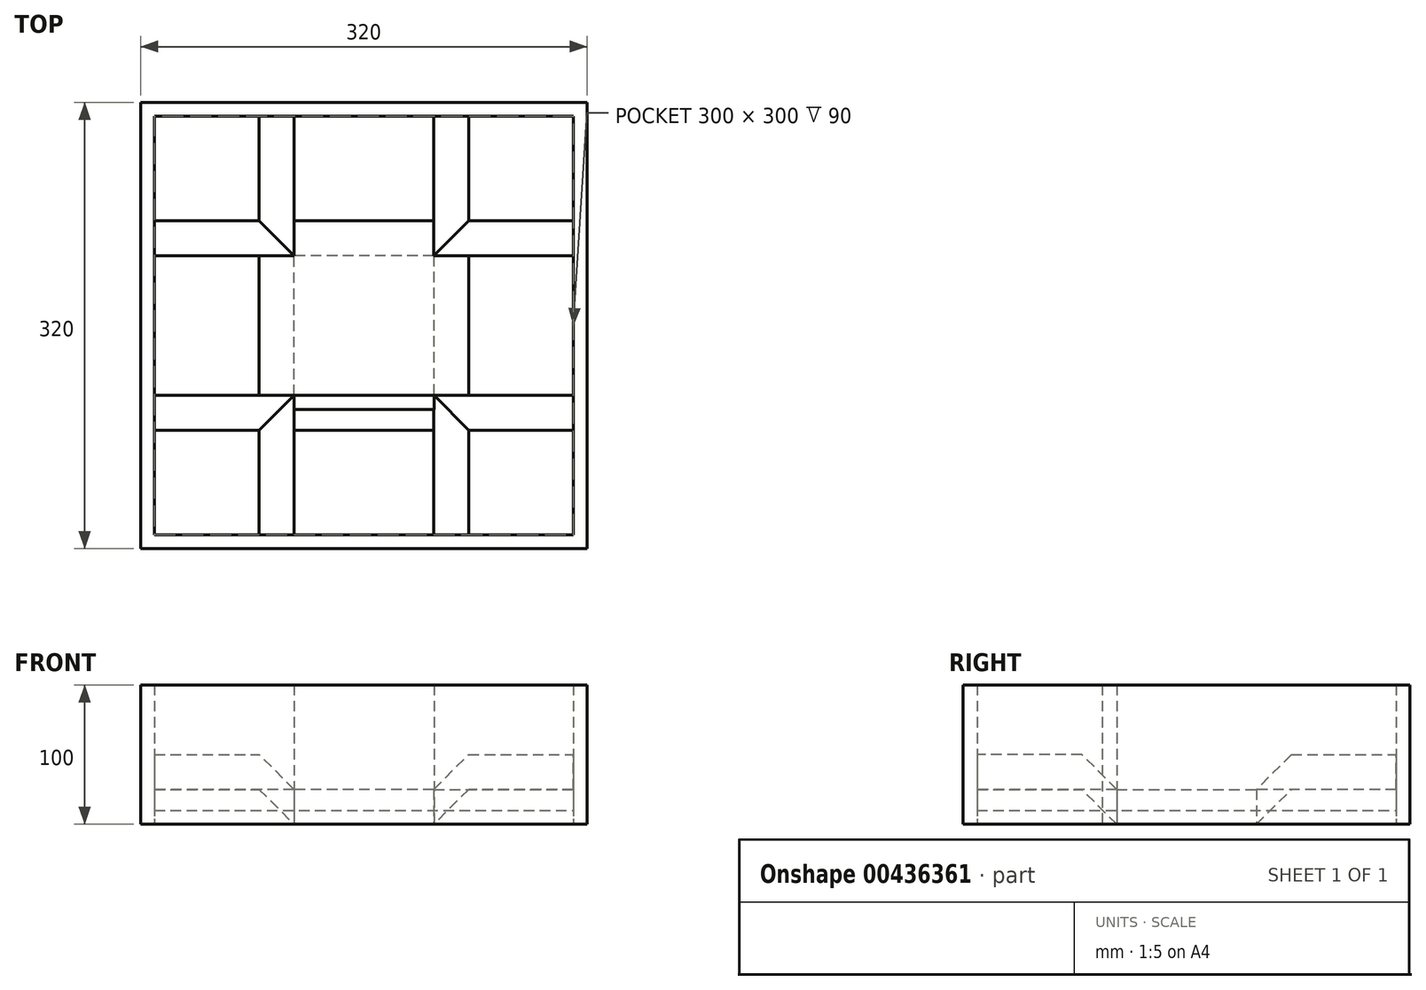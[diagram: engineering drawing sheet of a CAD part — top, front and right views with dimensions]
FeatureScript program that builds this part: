
annotation { "Feature Type Name" : "Feature", "Feature Type Description" : "" }
export const myFeature = defineFeature(function(context is Context, id is Id, definition is map)
    precondition{}
    {
        {
            var Q0;
            Q0=qCreatedBy(makeId("Top.planeOp"),FACE);
            var sketch = newSketch(context, id + "F0", { "sketchPlane" : qUnion([Q0])});
            skLineSegment(sketch, "E0", {"start": v(0, 0) * mm, "end": v(100, 0) * mm});
            skLineSegment(sketch, "E1", {"start": v(100, 0) * mm, "end": v(100, 100) * mm});
            skLineSegment(sketch, "E2", {"start": v(100, 100) * mm, "end": v(200, 100) * mm});
            skLineSegment(sketch, "E3", {"start": v(200, 100) * mm, "end": v(200, 0) * mm});
            skLineSegment(sketch, "E4", {"start": v(200, 0) * mm, "end": v(300, 0) * mm});
            skLineSegment(sketch, "E5", {"start": v(300, 0) * mm, "end": v(300, -100) * mm});
            skLineSegment(sketch, "E6", {"start": v(300, -100) * mm, "end": v(200, -100) * mm});
            skLineSegment(sketch, "E7", {"start": v(200, -100) * mm, "end": v(200, -200) * mm});
            skLineSegment(sketch, "E8", {"start": v(200, -200) * mm, "end": v(100, -200) * mm});
            skLineSegment(sketch, "E9", {"start": v(100, -200) * mm, "end": v(100, -100) * mm});
            skLineSegment(sketch, "E10", {"start": v(100, -100) * mm, "end": v(0, -100) * mm});
            skLineSegment(sketch, "E11", {"start": v(0, -100) * mm, "end": v(0, 0) * mm});
            skLineSegment(sketch, "E12", {"start": v(100, -100) * mm, "end": v(200, -100) * mm});
            skLineSegment(sketch, "E13", {"start": v(200, 0) * mm, "end": v(200, -100) * mm});
            skLineSegment(sketch, "E14", {"start": v(200, 0) * mm, "end": v(100, 0) * mm});
            skLineSegment(sketch, "E15", {"start": v(100, -100) * mm, "end": v(100, 0) * mm});
            skSolve(sketch);
        }
        {
            var Q0;
            Q0=makeQuery(id+"F0.imprint","IMPRINT",FACE,{"disambiguationData":[TD([[makeQuery(id+"F0.imprint","IMPRINT",EDGE,{"derivedFrom":sQuery(id+"F0.wireOp",EDGE,"E1")}),-1.0]])]});
            var Q1;
            Q1=makeQuery(id+"F0.imprint","IMPRINT",FACE,{"disambiguationData":[TD([[makeQuery(id+"F0.imprint","IMPRINT",EDGE,{"derivedFrom":sQuery(id+"F0.wireOp",EDGE,"E0")}),-1.0]])]});
            var Q2;
            Q2=makeQuery(id+"F0.imprint","IMPRINT",FACE,{"disambiguationData":[TD([[makeQuery(id+"F0.imprint","IMPRINT",EDGE,{"derivedFrom":sQuery(id+"F0.wireOp",EDGE,"E7")}),-1.0]])]});
            var Q3;
            Q3=makeQuery(id+"F0.imprint","IMPRINT",FACE,{"disambiguationData":[TD([[makeQuery(id+"F0.imprint","IMPRINT",EDGE,{"derivedFrom":sQuery(id+"F0.wireOp",EDGE,"E4")}),-1.0]])]});
            extrude(context, id + "F1", {"entities" : qUnion([Q0, Q1, Q2, Q3]), "depth" : 25 * mm});
        }
        {
            var Q0;
            Q0=makeQuery(id+"F1.opExtrude","CAP_FACE",FACE,{"disambiguationData":[OSD([sQuery(id+"F0.wireOp",EDGE,"E7"),sQuery(id+"F0.wireOp",EDGE,"E8"),sQuery(id+"F0.wireOp",EDGE,"E9"),sQuery(id+"F0.wireOp",EDGE,"E12")])],"isStart":true});
            var sketch = newSketch(context, id + "F2", { "sketchPlane" : qUnion([Q0])});
            skLineSegment(sketch, "E16.bottom", {"start": v(0, 0) * mm, "end": v(100, 0) * mm});
            skLineSegment(sketch, "E16.top", {"start": v(0, -100) * mm, "end": v(100, -100) * mm});
            skLineSegment(sketch, "E16.left", {"start": v(0, 0) * mm, "end": v(0, -100) * mm});
            skLineSegment(sketch, "E16.right", {"start": v(100, 0) * mm, "end": v(100, -100) * mm});
            skLineSegment(sketch, "E17.bottom", {"start": v(100, 100) * mm, "end": v(0, 100) * mm});
            skLineSegment(sketch, "E17.top", {"start": v(100, 200) * mm, "end": v(0, 200) * mm});
            skLineSegment(sketch, "E17.left", {"start": v(100, 100) * mm, "end": v(100, 200) * mm});
            skLineSegment(sketch, "E17.right", {"start": v(0, 100) * mm, "end": v(0, 200) * mm});
            skLineSegment(sketch, "E18.bottom", {"start": v(200, 100) * mm, "end": v(300, 100) * mm});
            skLineSegment(sketch, "E18.top", {"start": v(200, 200) * mm, "end": v(300, 200) * mm});
            skLineSegment(sketch, "E18.left", {"start": v(200, 100) * mm, "end": v(200, 200) * mm});
            skLineSegment(sketch, "E18.right", {"start": v(300, 100) * mm, "end": v(300, 200) * mm});
            skLineSegment(sketch, "E19.bottom", {"start": v(200, 0) * mm, "end": v(300, 0) * mm});
            skLineSegment(sketch, "E19.top", {"start": v(200, -100) * mm, "end": v(300, -100) * mm});
            skLineSegment(sketch, "E19.left", {"start": v(200, 0) * mm, "end": v(200, -100) * mm});
            skLineSegment(sketch, "E19.right", {"start": v(300, 0) * mm, "end": v(300, -100) * mm});
            skSolve(sketch);
        }
        {
            var Q0;
            Q0=makeQuery(id+"F2.imprint","IMPRINT",FACE,{"disambiguationData":[TD([[makeQuery(id+"F2.imprint","IMPRINT",EDGE,{"derivedFrom":sQuery(id+"F2.wireOp",EDGE,"E16.bottom")}),-1.0]])]});
            var Q1;
            Q1=makeQuery(id+"F2.imprint","IMPRINT",FACE,{"disambiguationData":[TD([[makeQuery(id+"F2.imprint","IMPRINT",EDGE,{"derivedFrom":sQuery(id+"F2.wireOp",EDGE,"E17.bottom")}),-1.0]])]});
            var Q2;
            Q2=makeQuery(id+"F2.imprint","IMPRINT",FACE,{"disambiguationData":[TD([[makeQuery(id+"F2.imprint","IMPRINT",EDGE,{"derivedFrom":sQuery(id+"F2.wireOp",EDGE,"E18.bottom")}),1.0]])]});
            var Q3;
            Q3=makeQuery(id+"F2.imprint","IMPRINT",FACE,{"disambiguationData":[TD([[makeQuery(id+"F2.imprint","IMPRINT",EDGE,{"derivedFrom":sQuery(id+"F2.wireOp",EDGE,"E19.bottom")}),-1.0]])]});
            extrude(context, id + "F3", {"entities" : qUnion([Q0, Q1, Q2, Q3]), "depth" : -50 * mm});
        }
        {
            var Q0;
            Q0=makeQuery(id+"F3.opExtrude","CAP_EDGE",EDGE,{"disambiguationData":[OSD([sQuery(id+"F2.wireOp",EDGE,"E17.left")])],"isStart":false});
            var Q1;
            Q1=makeQuery(id+"F3.opExtrude","CAP_EDGE",EDGE,{"disambiguationData":[OSD([sQuery(id+"F2.wireOp",EDGE,"E17.bottom")])],"isStart":false});
            var Q2;
            Q2=makeQuery(id+"F3.opExtrude","CAP_EDGE",EDGE,{"disambiguationData":[OSD([sQuery(id+"F2.wireOp",EDGE,"E16.bottom")])],"isStart":false});
            var Q3;
            Q3=makeQuery(id+"F3.opExtrude","CAP_EDGE",EDGE,{"disambiguationData":[OSD([sQuery(id+"F2.wireOp",EDGE,"E16.right")])],"isStart":false});
            var Q4;
            Q4=makeQuery(id+"F3.opExtrude","CAP_EDGE",EDGE,{"disambiguationData":[OSD([sQuery(id+"F2.wireOp",EDGE,"E19.left")])],"isStart":false});
            var Q5;
            Q5=makeQuery(id+"F3.opExtrude","CAP_EDGE",EDGE,{"disambiguationData":[OSD([sQuery(id+"F2.wireOp",EDGE,"E19.bottom")])],"isStart":false});
            var Q6;
            Q6=makeQuery(id+"F3.opExtrude","CAP_EDGE",EDGE,{"disambiguationData":[OSD([sQuery(id+"F2.wireOp",EDGE,"E18.bottom")])],"isStart":false});
            var Q7;
            Q7=makeQuery(id+"F3.opExtrude","CAP_EDGE",EDGE,{"disambiguationData":[OSD([sQuery(id+"F2.wireOp",EDGE,"E18.left")])],"isStart":false});
            var Q8;
            Q8=makeQuery(id+"F1.opExtrude","CAP_EDGE",EDGE,{"disambiguationData":[OSD([sQuery(id+"F0.wireOp",EDGE,"E12")])],"isStart":false});
            var Q9;
            Q9=makeQuery(id+"F1.opExtrude","CAP_EDGE",EDGE,{"disambiguationData":[OSD([sQuery(id+"F0.wireOp",EDGE,"E15")])],"isStart":false});
            var Q10;
            Q10=makeQuery(id+"F1.opExtrude","CAP_EDGE",EDGE,{"disambiguationData":[OSD([sQuery(id+"F0.wireOp",EDGE,"E14")])],"isStart":false});
            var Q11;
            Q11=makeQuery(id+"F1.opExtrude","CAP_EDGE",EDGE,{"disambiguationData":[OSD([sQuery(id+"F0.wireOp",EDGE,"E13")])],"isStart":false});
            chamfer(context, id + "F4", {"entities" : qUnion([Q0, Q1, Q2, Q3, Q4, Q5, Q6, Q7, Q8, Q9, Q10, Q11]), "width" : 25 * mm, "tangentPropagation" : true});
        }
        {
            var Q0;
            Q0=qCreatedBy(makeId("Top.planeOp"),FACE);
            var sketch = newSketch(context, id + "F5", { "sketchPlane" : qUnion([Q0])});
            skLineSegment(sketch, "E20", {"start": v(-10, 0) * mm, "end": v(-10, 110) * mm});
            skLineSegment(sketch, "E21.bottom", {"start": v(-10, 110) * mm, "end": v(310, 110) * mm});
            skLineSegment(sketch, "E21.top", {"start": v(-10, -210) * mm, "end": v(310, -210) * mm});
            skLineSegment(sketch, "E21.left", {"start": v(-10, 110) * mm, "end": v(-10, -210) * mm});
            skLineSegment(sketch, "E21.right", {"start": v(310, 110) * mm, "end": v(310, -210) * mm});
            skSolve(sketch);
        }
        {
            var Q0;
            {var subQ0=sQuery(id+"F5.wireOp",EDGE,"E21.bottom");Q0=makeQuery(id+"F5.imprint","IMPRINT",FACE,{"disambiguationData":[TD([[makeQuery(id+"F5.imprint","IMPRINT",EDGE,{"derivedFrom":subQ0}),-1.0]])]});}
            extrude(context, id + "F6", {"entities" : qUnion([Q0]), "depth" : 100 * mm});
        }
        {
            var Q0;
            Q0=makeQuery(id+"F6.opExtrude","CAP_FACE",FACE,{"disambiguationData":[OSD([sQuery(id+"F5.wireOp",EDGE,"E21.bottom"),sQuery(id+"F5.wireOp",EDGE,"E21.top"),sQuery(id+"F5.wireOp",EDGE,"E21.left"),sQuery(id+"F5.wireOp",EDGE,"E21.right")])],"isStart":false});
            shell(context, id + "F7", {"entities" : qUnion([Q0]), "thickness" : 10 * mm});
        }
        {
            var Q0;
            Q0=qCreatedBy(makeId("Top.planeOp"),FACE);
            var sketch = newSketch(context, id + "F8", { "sketchPlane" : qUnion([Q0])});
            skLineSegment(sketch, "E22.bottom", {"start": v(100.07, -100.04) * mm, "end": v(200.16, -100.04) * mm});
            skLineSegment(sketch, "E22.top", {"start": v(100.07, -110.32) * mm, "end": v(200.16, -110.32) * mm});
            skLineSegment(sketch, "E22.left", {"start": v(100.07, -100.04) * mm, "end": v(100.07, -110.32) * mm});
            skLineSegment(sketch, "E22.right", {"start": v(200.16, -100.04) * mm, "end": v(200.16, -110.32) * mm});
            skSolve(sketch);
        }
        {
            var Q0;
            Q0 = qSketchRegion(id + "F8", true);
            extrude(context, id + "F9", {"entities" : qUnion([Q0]), "depth" : 100 * mm});
        }
    });
